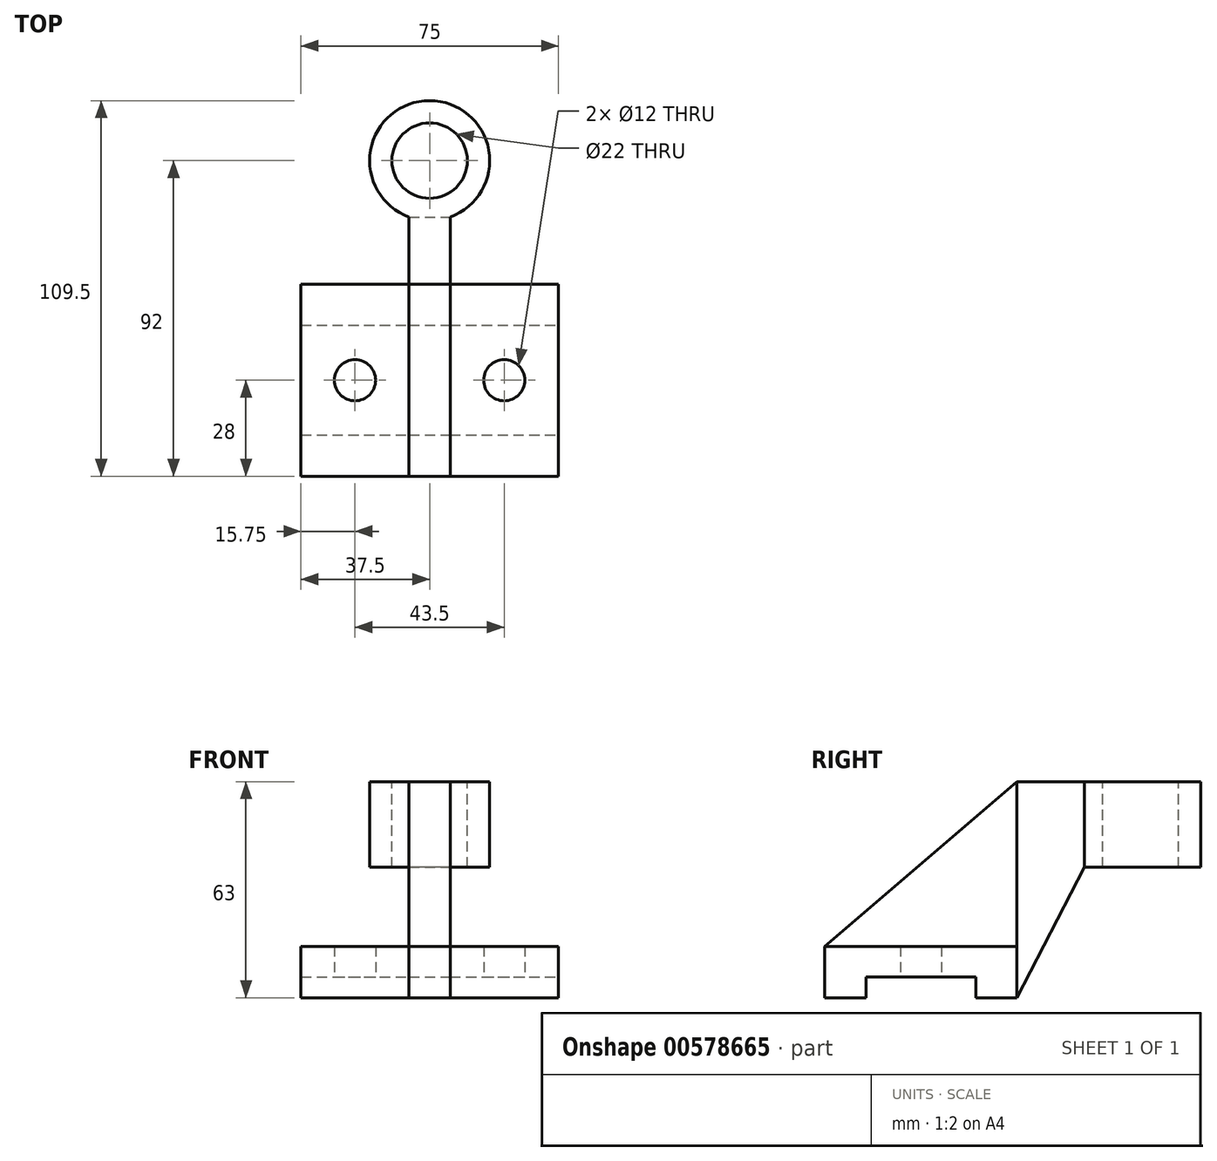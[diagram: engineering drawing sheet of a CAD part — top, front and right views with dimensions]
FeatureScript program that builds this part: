
annotation { "Feature Type Name" : "Feature", "Feature Type Description" : "" }
export const myFeature = defineFeature(function(context is Context, id is Id, definition is map)
    precondition{}
    {
        {
            var Q0;
            Q0=qCreatedBy(makeId("Top.planeOp"),FACE);
            var sketch = newSketch(context, id + "F0", { "sketchPlane" : qUnion([Q0])});
            skLineSegment(sketch, "E0.bottom", {"start": v(37.5, 28) * mm, "end": v(-37.5, 28) * mm});
            skLineSegment(sketch, "E0.top", {"start": v(37.5, -28) * mm, "end": v(-37.5, -28) * mm});
            skLineSegment(sketch, "E0.left", {"start": v(37.5, 28) * mm, "end": v(37.5, -28) * mm});
            skLineSegment(sketch, "E0.right", {"start": v(-37.5, 28) * mm, "end": v(-37.5, -28) * mm});
            skPoint(sketch, "E0.middle", {"position": v(0, 0) * mm});
            skLineSegment(sketch, "E1", {"start": v(0, 28) * mm, "end": v(0, -28) * mm});
            skLineSegment(sketch, "E2", {"start": v(-6, 28) * mm, "end": v(-6, -28) * mm});
            skLineSegment(sketch, "E3", {"start": v(6, 28) * mm, "end": v(6, -28) * mm});
            skLineSegment(sketch, "E4", {"start": v(-6, 28) * mm, "end": v(-37.5, 28) * mm});
            skLineSegment(sketch, "E5", {"start": v(6, 28) * mm, "end": v(37.5, 28) * mm});
            skCircle(sketch, "E6", {"center": v(-21.75, 0) * mm, "radius": 6 * mm});
            skPoint(sketch, "E6.centerSnap0", {"position": v(-21.75, 28) * mm});
            skCircle(sketch, "E7.MirrorC", {"center": v(21.75, 0) * mm, "radius": 6 * mm});
            skSolve(sketch);
        }
        {
            var Q0;
            {var subQ1=sQuery(id+"F0.wireOp",EDGE,"E0.right");Q0=makeQuery(id+"F0.imprint","IMPRINT",FACE,{"disambiguationData":[TD([[makeQuery(id+"F0.imprint","IMPRINT",EDGE,{"derivedFrom":subQ1}),1.0]])]});}
            var Q1;
            {var subQ1=sQuery(id+"F0.wireOp",EDGE,"E0.left");Q1=makeQuery(id+"F0.imprint","IMPRINT",FACE,{"disambiguationData":[TD([[makeQuery(id+"F0.imprint","IMPRINT",EDGE,{"derivedFrom":subQ1}),-1.0]])]});}
            extrude(context, id + "F1", {"entities" : qUnion([Q0, Q1]), "depth" : 15 * mm, "offsetDistance" : 25 * mm});
        }
        {
            var Q0;
            {var subQ2=sQuery(id+"F0.wireOp",EDGE,"E1");Q0=makeQuery(id+"F0.imprint","IMPRINT",FACE,{"disambiguationData":[TD([[makeQuery(id+"F0.imprint","IMPRINT",EDGE,{"derivedFrom":subQ2}),-1.0]])]});}
            var Q1;
            {var subQ2=sQuery(id+"F0.wireOp",EDGE,"E1");Q1=makeQuery(id+"F0.imprint","IMPRINT",FACE,{"disambiguationData":[TD([[makeQuery(id+"F0.imprint","IMPRINT",EDGE,{"derivedFrom":subQ2}),1.0]])]});}
            extrude(context, id + "F2", {"entities" : qUnion([Q0, Q1]), "depth" : 63 * mm, "offsetDistance" : 25 * mm});
        }
        {
            var Q0;
            Q0=makeQuery(id+"F2.opExtrude","SWEPT_FACE",FACE,{"disambiguationData":[OSD([sQuery(id+"F0.wireOp",EDGE,"E3")])]});
            var sketch = newSketch(context, id + "F3", { "sketchPlane" : qUnion([Q0])});
            skLineSegment(sketch, "E8.0.0", {"start": v(-28, 0) * mm, "end": v(28, 0) * mm});
            skLineSegment(sketch, "E8.0.1", {"start": v(28, 0) * mm, "end": v(28, 63) * mm});
            skLineSegment(sketch, "E8.0.2", {"start": v(28, 63) * mm, "end": v(-28, 63) * mm});
            skLineSegment(sketch, "E8.0.3", {"start": v(-28, 63) * mm, "end": v(-28, 0) * mm});
            skLineSegment(sketch, "E9.0", {"start": v(28, 15) * mm, "end": v(-28, 15) * mm});
            skLineSegment(sketch, "E10", {"start": v(28, 63) * mm, "end": v(-28, 15) * mm});
            skSolve(sketch);
        }
        {
            var Q0;
            {var subQ0=sQuery(id+"F3.wireOp",EDGE,"E8.0.2");Q0=makeQuery(id+"F3.imprint","IMPRINT",FACE,{"disambiguationData":[TD([[makeQuery(id+"F3.imprint","IMPRINT",EDGE,{"derivedFrom":subQ0}),1.0]])]});}
            extrude(context, id + "F4", {"entities" : qUnion([Q0]), "operationType" : NewBodyOperationType.REMOVE, "oppositeDirection" : true, "depth" : 25 * mm, "offsetDistance" : 25 * mm});
        }
        {
            var Q0;
            Q0=makeQuery(id+"F2.opExtrude","SWEPT_FACE",FACE,{"disambiguationData":[OSD([sQuery(id+"F0.wireOp",EDGE,"E0.bottom")])]});
            var sketch = newSketch(context, id + "F5", { "sketchPlane" : qUnion([Q0])});
            skSolve(sketch);
        }
        {
            var Q0;
            Q0 = qSketchRegion(id + "F5", true);
            var Q1;
            {var subQ0=sQuery(id+"F0.wireOp",EDGE,"E0.bottom");Q1=makeQuery(id+"F5.imprint","IMPRINT",FACE,{"disambiguationData":[TD([[makeQuery(id+"F5.imprint","IMPRINT",EDGE,{"derivedFrom":makeQuery(id+"F2.opExtrude","CAP_EDGE",EDGE,{"disambiguationData":[OSD([subQ0])],"isStart":true})}),1.0]])]});}
            extrude(context, id + "F6", {"entities" : qUnion([Q0, Q1]), "depth" : 36 * mm, "offsetDistance" : 25 * mm});
        }
        {
            var Q0;
            Q0=makeQuery(id+"F6.opExtrude","SWEPT_FACE",FACE,{"disambiguationData":[OSD([sQuery(id+"F0.wireOp",EDGE,"E0.bottom"),sQuery(id+"F3.wireOp",EDGE,"E8.0.1"),sQuery(id+"F3.wireOp",EDGE,"E8.0.2"),sQuery(id+"F3.wireOp",EDGE,"E10")])]});
            var sketch = newSketch(context, id + "F7", { "sketchPlane" : qUnion([Q0])});
            skCircle(sketch, "E11", {"center": v(0, 64) * mm, "radius": 11 * mm});
            skCircle(sketch, "E12", {"center": v(0, 64) * mm, "radius": 17.5 * mm});
            skSolve(sketch);
        }
        {
            var Q0;
            {var subQ1=sQuery(id+"F3.wireOp",EDGE,"E10");var subQ2=sQuery(id+"F3.wireOp",EDGE,"E8.0.2");var subQ3=sQuery(id+"F3.wireOp",EDGE,"E8.0.1");var subQ4=sQuery(id+"F0.wireOp",EDGE,"E0.bottom");var subQ9=makeQuery(id+"F6.opExtrude","CAP_EDGE",EDGE,{"disambiguationData":[OSD([subQ4,subQ3,subQ2,subQ1])],"isStart":false});Q0=makeQuery(id+"F7.imprint","IMPRINT",FACE,{"disambiguationData":[TD([[makeQuery(id+"F7.imprint","IMPRINT",EDGE,{"derivedFrom":subQ9}),1.0]])]});}
            extrude(context, id + "F8", {"entities" : qUnion([Q0]), "operationType" : NewBodyOperationType.REMOVE, "oppositeDirection" : true, "depth" : 134.4 * mm, "offsetDistance" : 25 * mm});
        }
        {
            var Q0;
            {var subQ0=sQuery(id+"F7.wireOp",EDGE,"E11");var subQ1=sQuery(id+"F3.wireOp",EDGE,"E10");var subQ2=sQuery(id+"F3.wireOp",EDGE,"E8.0.2");var subQ3=sQuery(id+"F3.wireOp",EDGE,"E8.0.1");var subQ4=sQuery(id+"F0.wireOp",EDGE,"E0.bottom");var subQ5=makeQuery(id+"F6.opExtrude","SWEPT_EDGE",EDGE,{"disambiguationData":[OSD([subQ4,sQuery(id+"F0.wireOp",EDGE,"E3"),sQuery(id+"F0.wireOp",EDGE,"E5"),subQ3,subQ2,subQ1])]});var subQ6=makeQuery(id+"F7.imprint","INTERSECT",VERTEX,{"derivedFrom":[subQ5,subQ0]});Q0=makeQuery(id+"F7.imprint","IMPRINT",FACE,{"disambiguationData":[TD([[makeQuery(id+"F7.imprint","IMPRINT",EDGE,{"disambiguationData":[TD([[subQ6,-1.0]])],"derivedFrom":subQ0}),-1.0]])]});}
            extrude(context, id + "F9", {"entities" : qUnion([Q0]), "operationType" : NewBodyOperationType.ADD, "oppositeDirection" : true, "depth" : 25 * mm, "offsetDistance" : 25 * mm});
        }
        {
            var Q0;
            Q0=makeQuery(id+"F6.opExtrude","SWEPT_FACE",FACE,{"disambiguationData":[OSD([sQuery(id+"F0.wireOp",EDGE,"E0.bottom"),sQuery(id+"F0.wireOp",EDGE,"E3"),sQuery(id+"F0.wireOp",EDGE,"E5")])]});
            var sketch = newSketch(context, id + "F10", { "sketchPlane" : qUnion([Q0])});
            skLineSegment(sketch, "E13.0.0", {"start": v(54.78, 0) * mm, "end": v(54.78, 38) * mm});
            skLineSegment(sketch, "E13.0.1", {"start": v(54.78, 38) * mm, "end": v(47.56, 38) * mm});
            skLineSegment(sketch, "E13.0.2", {"start": v(47.56, 38) * mm, "end": v(47.56, 63) * mm});
            skLineSegment(sketch, "E13.0.3", {"start": v(47.56, 63) * mm, "end": v(28, 63) * mm});
            skLineSegment(sketch, "E13.0.4", {"start": v(28, 63) * mm, "end": v(28, 0) * mm});
            skLineSegment(sketch, "E13.0.5", {"start": v(28, 0) * mm, "end": v(54.78, 0) * mm});
            skLineSegment(sketch, "E14.0", {"start": v(28, 15) * mm, "end": v(-28, 15) * mm});
            skLineSegment(sketch, "E15", {"start": v(47.56, 38) * mm, "end": v(28, 0) * mm});
            skSolve(sketch);
        }
        {
            var Q0;
            Q0=makeQuery(id+"F10.imprint","IMPRINT",FACE,{"disambiguationData":[TD([[makeQuery(id+"F10.imprint","IMPRINT",EDGE,{"derivedFrom":sQuery(id+"F10.wireOp",EDGE,"E13.0.0")}),1.0]])]});
            extrude(context, id + "F11", {"entities" : qUnion([Q0]), "operationType" : NewBodyOperationType.REMOVE, "oppositeDirection" : true, "depth" : 25 * mm, "offsetDistance" : 25 * mm});
        }
        {
            var Q0;
            Q0=makeQuery(id+"F1.opExtrude","SWEPT_FACE",FACE,{"disambiguationData":[OSD([sQuery(id+"F0.wireOp",EDGE,"E0.left")])]});
            var sketch = newSketch(context, id + "F12", { "sketchPlane" : qUnion([Q0])});
            skLineSegment(sketch, "E16.bottom", {"start": v(-16, 0) * mm, "end": v(16, 0) * mm});
            skLineSegment(sketch, "E16.top", {"start": v(-16, 6) * mm, "end": v(16, 6) * mm});
            skLineSegment(sketch, "E16.left", {"start": v(-16, 0) * mm, "end": v(-16, 6) * mm});
            skLineSegment(sketch, "E16.right", {"start": v(16, 0) * mm, "end": v(16, 6) * mm});
            skSolve(sketch);
        }
        {
            var Q0;
            Q0 = qSketchRegion(id + "F12", true);
            extrude(context, id + "F13", {"entities" : qUnion([Q0]), "operationType" : NewBodyOperationType.REMOVE, "oppositeDirection" : true, "depth" : 101.3 * mm, "offsetDistance" : 25 * mm});
        }
    });
